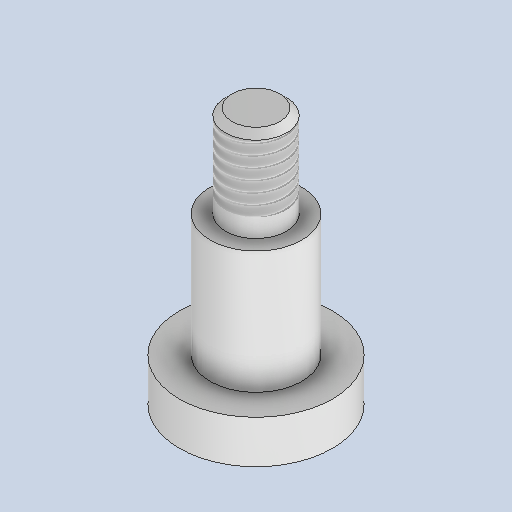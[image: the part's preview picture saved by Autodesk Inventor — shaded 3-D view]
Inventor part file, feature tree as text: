
AUTODESK INVENTOR PART (.ipt)
format: ipt  version: 2024.2 (Build 282272000, 272)  size: 290,304 bytes
history: native  units: mm
features: sketch x2, revolve x1, thread x1, extrude x1, chamfer x1
ambient origin geometry x8: Origin, YZ Plane, XZ Plane, XY Plane, X Axis, Y Axis, Z Axis, Center Point
bodies: Solid1 (feature_tree)
feature tree (6):
  revolve  "Revolution1"  [1 undecoded]
  thread  "Thread1"  [1 undecoded]
  extrude  "Extrusion1"  Depth=8.0mm
  chamfer  "Chamfer1"  Distance=2.8mm
  sketch  "Sketch1"  dims[d0=10.0mm d1=6.0mm d2=4.0mm]
  sketch  "Sketch2"  dims[d3=6.0mm d4=8.0mm d5=2.8mm d6=90.0deg d7=6.0mm d8=1.2mm d9=2.5mm d10=2.0mm d11=0.0mm d12=0.43mm d13=2.0mm d14=45.0deg]
note: 2 required parameter values undecoded (feature->parameter linkage not recoverable at this tier; creation-order binding heuristic only, values carry confidence <= 0.55)